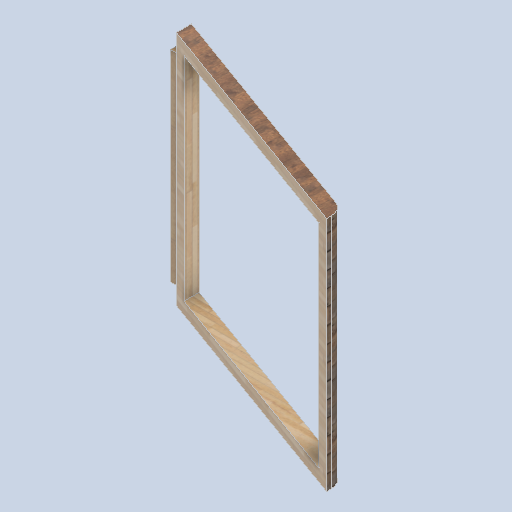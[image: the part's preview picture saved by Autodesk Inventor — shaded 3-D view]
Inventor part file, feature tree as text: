
AUTODESK INVENTOR PART (.ipt)
format: ipt  version: 2024.2 (Build 282272000, 272)  size: 165,888 bytes
history: native  units: in
note: dims shown in document units (in); Inventor stores cm internally (conversion verified against a paired STEP export)
features: sketch x5, other x3, plane x1
ambient origin geometry x8: Origin, YZ Plane, XZ Plane, XY Plane, X Axis, Y Axis, Z Axis, Center Point
bodies: Solid1 (feature_tree)
feature tree (9):
  other  "side_curve_frame_01.ipt"
  other  "Solid1::side_curve_frame_01.ipt"
  other  "TaggingFeature1"
  sketch  "Sketch1"  dims[d0=0.3937in]
  sketch  "Sketch2"
  sketch  "Sketch3"
  sketch  "Sketch4"
  sketch  "Sketch5"
  plane  "Work Plane1"
